# Revit family: Шкаф телекоммуникационный настенный разборный 19” 600x650_1
name_source: partatom
category: Обобщенные модели
units: mm (PartAtom-declared; Revit-internal decimal feet)

## family parameters
Может служить основой для арматурных стержней = Нет
Общий = Нет
Основа = Грань
При загрузке вырезать с полостями = Нет
Размер круглого соединителя = Использовать диаметр
Тип детали = Нормальный
Точка расчета площади = Нет

## types (15) — shared parameters
ADSK_URL документации изделия = https://www.ssd.ru
ADSK_URL страницы изделия = https://www.ssd.ru
ADSK_Единица измерения = шт
ADSK_Завод-изготовитель = АО СВЯЗЬСТРОЙДЕТАЛЬ
ADSK_Зона = -
ADSK_Количество = 1
ADSK_Материал обозначение = Серый RAL 7035
ADSK_Предел огнестойкости = -
ADSK_Размер_Глубина = 650 мм
ADSK_Размер_Ширина = 600 мм
Смещение двери = 626 мм

## per-type parameters (varying)
| type | ADSK_Код изделия | ADSK_Масса_Текст | ADSK_Наименование | ADSK_Размер_Высота | Высота двери | Дверь | Отметка по умолчанию |
| ШТ-НСр 6U (600х650мм) стеклянная дверь | 130411-00551 | 21,1 | Шкаф телекоммуникационный настенный разборный 19”,6U(600x650), ШТ-НСр-6U-600-650-С дверь стекло ССД | 360 мм | 280 мм | Дверь_С | 800 мм |
| ШТ-НСр 6U (600х650мм) металлическая дверь | 130411-00552 | 20,7 | Шкаф телекоммуникационный настенный разборный 19”,6U(600x650), ШТ-НСр-6U-600-650-М дверь металл ССД | 360 мм | 280 мм | Дверь_М | 800 мм |
| ШТ-НСр 6U (600х650мм) перфорированная дверь | 130411-00553 | 20,4 | Шкаф телекоммуникационный настенный разборный 19”,6U(600x650), ШТ-НСр-6U-600-650-П дверь перфорированная ССД | 360 мм | 280 мм | Дверь_П-6U | 800 мм |
| ШТ-НСр 9U (600х650мм) стеклянная дверь | 130411-00560 | 24,3 | Шкаф телекоммуникационный настенный разборный 19”,9U(600x650), ШТ-НСр-9U-600-650-С дверь стекло ССД | 493 мм | 413 мм | Дверь_С | 800 мм |
| ШТ-НСр 9U (600х650мм) металлическая дверь | 130411-00561 | 23,8 | Шкаф телекоммуникационный настенный разборный 19”,9U(600x650), ШТ-НСр-9U-600-650-М дверь металл ССД | 493 мм | 413 мм | Дверь_М | 800 мм |
| ШТ-НСр 9U (600х650мм) перфорированная дверь | 130411-00562 | 23,5 | Шкаф телекоммуникационный настенный разборный 19”,9U(600x650), ШТ-НСр-9U-600-650-П дверь перфорированная ССД | 493 мм | 413 мм | Дверь_П-9U | 800 мм |
| ШТ-НСр 12U (600х650мм) стеклянная дверь | 130411-00569 | 27,7 | Шкаф телекоммуникационный настенный разборный 19”,12U(600x650), ШТ-НСр-12U-600-650-С дверь стекло ССД | 626 мм | 546 мм | Дверь_С | 0 мм |
| ШТ-НСр 12U (600х650мм) металлическая двер | 130411-00570 | 23,6 | Шкаф телекоммуникационный настенный разборный 19”,12U(600x650), ШТ-НСр-12U-600-650-М дверь металл ССД | 626 мм | 546 мм | Дверь_М | 800 мм |
| ШТ-НСр 12U (600х650мм) перфорированная дверь | 130411-00571 | 26,6 | Шкаф телекоммуникационный настенный разборный 19”,12U(600x650), ШТ-НСр-12U-600-650-П дверь перфорированная ССД | 626 мм | 546 мм | Дверь_П-12U | 800 мм |
| ШТ-НСр 15U (600х650мм) стеклянная дверь | 130411-00578 | 31,0 | Шкаф телекоммуникационный настенный разборный 19”,15U(600x650), ШТ-НСр-15U-600-650-С дверь стекло ССД | 760 мм | 680 мм | Дверь_С | 800 мм |
| ШТ-НСр 15U (600х650мм) металлическая дверь | 130411-00579 | 30,0 | Шкаф телекоммуникационный настенный разборный 19”,15U(600x650), ШТ-НСр-15U-600-650-М дверь металл ССД | 760 мм | 680 мм | Дверь_М | 800 мм |
| ШТ-НСр 15U (600х650мм) перфорированная дверь | 130411-00580 | 29,7 | Шкаф телекоммуникационный настенный разборный 19”,15U(600x650), ШТ-НСр-15U-600-650-П дверь перфорированная ССД | 760 мм | 680 мм | Дверь_П-15U | 800 мм |
| ШТ-НСр 18U (600х650мм) стеклянная дверь | 130411-00587 | 34,2 | Шкаф телекоммуникационный настенный разборный 19”,18U(600x650), ШТ-НСр-18U-600-650-С дверь стекло ССД | 893 мм | 813 мм | Дверь_С | 800 мм |
| ШТ-НСр 18U (600х650мм) металлическая дверь | 130411-00588 | 33,1 | Шкаф телекоммуникационный настенный разборный 19”,18U(600x650), ШТ-НСр-18U-600-650-М дверь металл ССД | 893 мм | 813 мм | Дверь_М | 800 мм |
| ШТ-НСр 18U (600х650мм) перфорированная дверь | 130411-00589 | 32,7 | Шкаф телекоммуникационный настенный разборный 19”,18U(600x650), ШТ-НСр-18U-600-650-П дверь перфорированная ССД | 893 мм | 813 мм | Дверь_П-18U | 800 мм |

note: column(s) folded — value = type name in every type: ADSK_Обозначение
